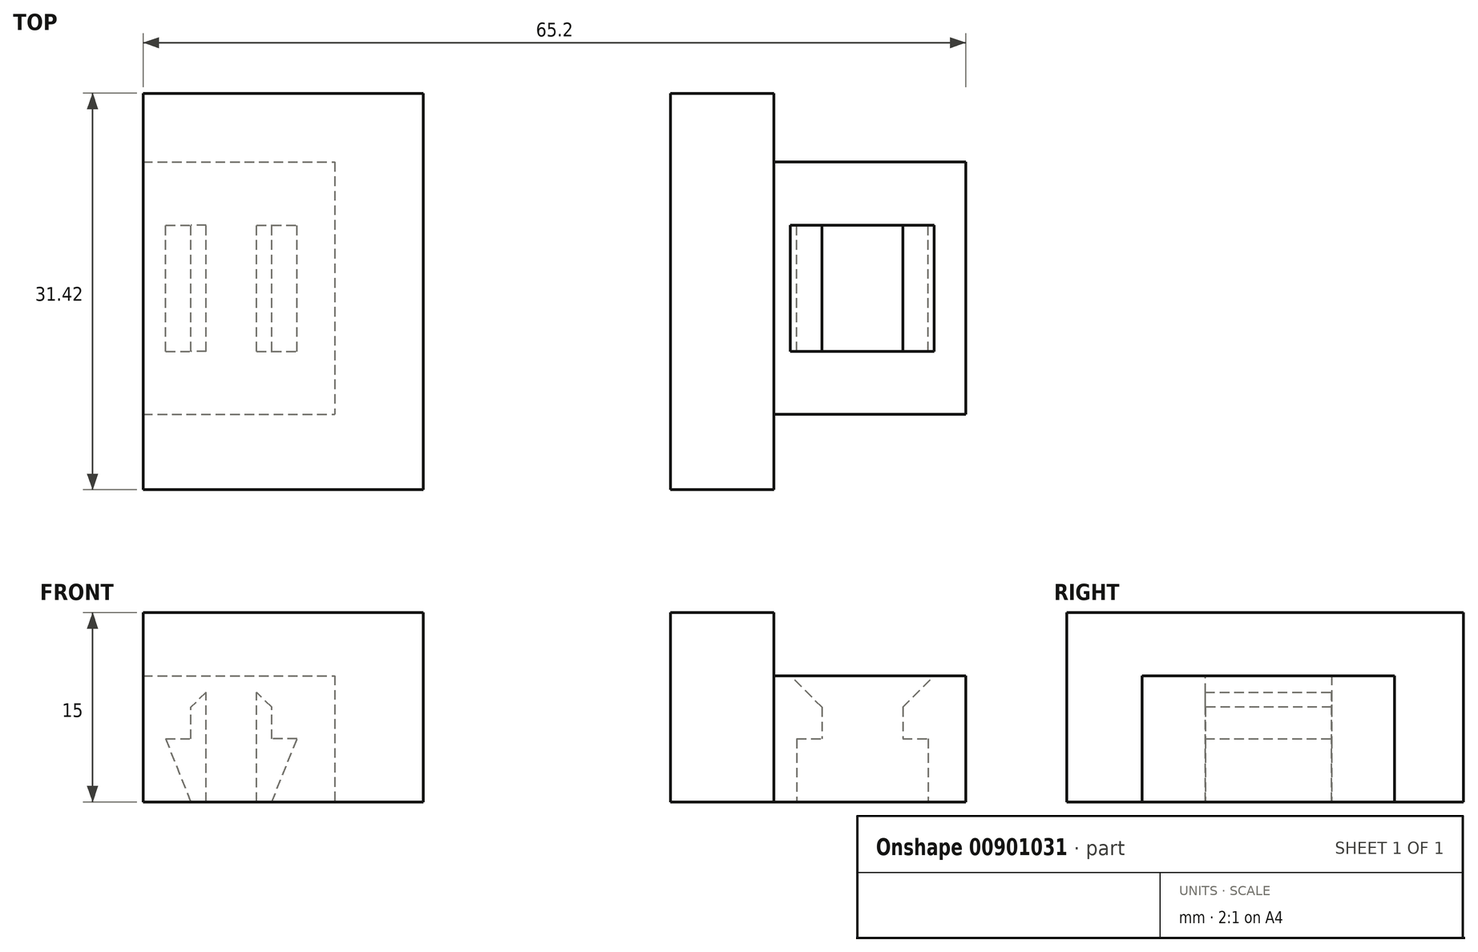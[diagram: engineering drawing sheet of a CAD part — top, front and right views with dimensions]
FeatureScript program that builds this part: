
annotation { "Feature Type Name" : "Feature", "Feature Type Description" : "" }
export const myFeature = defineFeature(function(context is Context, id is Id, definition is map)
    precondition{}
    {
        {
            assignVariable(context, id + "F0", {"name" : "depth", "anyValue" : 10 * mm});
        }
        {
            assignVariable(context, id + "F1", {"name" : "width", "anyValue" : 10 * mm});
        }
        {
            assignVariable(context, id + "F2", {"name" : "front", "anyValue" : 5 * mm});
        }
        {
            var Q0;
            Q0=qCreatedBy(makeId("Front.planeOp"),FACE);
            var sketch = newSketch(context, id + "F3", { "sketchPlane" : qUnion([Q0])});
            skLineSegment(sketch, "E0", {"start": v(0, -1.02) * mm, "end": v(0, 5.37) * mm, "construction": true});
            skLineSegment(sketch, "E1.bottom", {"start": v(-2, 0) * mm, "end": v(-3.2, 0) * mm});
            skLineSegment(sketch, "E1.top", {"start": v(-2, 10) * mm, "end": v(-3.2, 10) * mm});
            skLineSegment(sketch, "E1.left", {"start": v(-2, 0) * mm, "end": v(-2, 10) * mm});
            skLineSegment(sketch, "E1.right", {"start": v(-3.2, 5) * mm, "end": v(-3.2, 10) * mm});
            skLineSegment(sketch, "E2", {"start": v(-3.2, 0) * mm, "end": v(-5.2, 5) * mm});
            skLineSegment(sketch, "E3", {"start": v(-5.2, 5) * mm, "end": v(-3.2, 5) * mm});
            skLineSegment(sketch, "E4.MirrorCS", {"start": v(5.2, 5) * mm, "end": v(3.2, 5) * mm});
            skLineSegment(sketch, "E5.MirrorCS", {"start": v(3.2, 5) * mm, "end": v(3.2, 10) * mm});
            skLineSegment(sketch, "E6.MirrorCS", {"start": v(2, 10) * mm, "end": v(3.2, 10) * mm});
            skLineSegment(sketch, "E7.MirrorCS", {"start": v(2, 0) * mm, "end": v(2, 10) * mm});
            skLineSegment(sketch, "E8.MirrorCS", {"start": v(2, 0) * mm, "end": v(3.2, 0) * mm});
            skLineSegment(sketch, "E9.MirrorCS", {"start": v(3.2, 0) * mm, "end": v(5.2, 5) * mm});
            skSolve(sketch);
        }
        {
            var Q0;
            Q0=makeQuery(id+"F3.imprint","IMPRINT",FACE,{"disambiguationData":[TD([[makeQuery(id+"F3.imprint","IMPRINT",EDGE,{"derivedFrom":sQuery(id+"F3.wireOp",EDGE,"E1.bottom")}),-1.0]])]});
            var Q1;
            Q1=makeQuery(id+"F3.imprint","IMPRINT",FACE,{"disambiguationData":[TD([[makeQuery(id+"F3.imprint","IMPRINT",EDGE,{"derivedFrom":sQuery(id+"F3.wireOp",EDGE,"E4.MirrorCS")}),1.0]])]});
            extrude(context, id + "F4", {"entities" : qUnion([Q0, Q1]), "depth" : getVariable(context, 'width'), "offsetDistance" : 25 * mm});
        }
        {
            var Q0;
            Q0=qCreatedBy(makeId("Top.planeOp"),FACE);
            var sketch = newSketch(context, id + "F5", { "sketchPlane" : qUnion([Q0])});
            skLineSegment(sketch, "E10.0", {"start": v(-3.2, -10) * mm, "end": v(-3.2, 0) * mm});
            skLineSegment(sketch, "E11.0", {"start": v(3.2, -10) * mm, "end": v(3.2, 0) * mm});
            skLineSegment(sketch, "E12", {"start": v(-3.2, 0) * mm, "end": v(3.2, 0) * mm});
            skLineSegment(sketch, "E13", {"start": v(-3.2, -10) * mm, "end": v(3.2, -10) * mm});
            skLineSegment(sketch, "E14.bottom", {"start": v(-7, 5) * mm, "end": v(15.2, 5) * mm});
            skLineSegment(sketch, "E14.top", {"start": v(-7, -15) * mm, "end": v(15.2, -15) * mm});
            skLineSegment(sketch, "E14.left", {"start": v(-7, 5) * mm, "end": v(-7, -15) * mm});
            skLineSegment(sketch, "E14.right", {"start": v(15.2, 5) * mm, "end": v(15.2, -15) * mm});
            skLineSegment(sketch, "E15", {"start": v(8.2, 5) * mm, "end": v(8.2, -15) * mm});
            skLineSegment(sketch, "E16.bottom", {"start": v(-7, 5) * mm, "end": v(-15.2, 5) * mm});
            skLineSegment(sketch, "E16.top", {"start": v(-7, -15.04) * mm, "end": v(-15.2, -15.04) * mm});
            skLineSegment(sketch, "E16.left", {"start": v(-7, 5) * mm, "end": v(-7, -15.04) * mm});
            skLineSegment(sketch, "E16.right", {"start": v(-15.2, 5) * mm, "end": v(-15.2, -15.04) * mm});
            skLineSegment(sketch, "E17.0", {"start": v(-5.2, -10) * mm, "end": v(-5.2, 0) * mm});
            skLineSegment(sketch, "E18.0", {"start": v(5.2, -10) * mm, "end": v(5.2, 0) * mm});
            skLineSegment(sketch, "E19", {"start": v(-5.2, 0) * mm, "end": v(5.2, 0) * mm});
            skLineSegment(sketch, "E20", {"start": v(-5.2, -10) * mm, "end": v(5.2, -10) * mm});
            skLineSegment(sketch, "E21.bottom", {"start": v(15.2, 5) * mm, "end": v(-7, 5) * mm});
            skLineSegment(sketch, "E21.top", {"start": v(15.2, 10.45) * mm, "end": v(-7, 10.45) * mm});
            skLineSegment(sketch, "E21.left", {"start": v(15.2, 5) * mm, "end": v(15.2, 10.45) * mm});
            skLineSegment(sketch, "E21.right", {"start": v(-7, 5) * mm, "end": v(-7, 10.45) * mm});
            skLineSegment(sketch, "E22.bottom", {"start": v(15.2, -15) * mm, "end": v(-7, -15) * mm});
            skLineSegment(sketch, "E22.top", {"start": v(15.2, -20.97) * mm, "end": v(-7, -20.97) * mm});
            skLineSegment(sketch, "E22.left", {"start": v(15.2, -15) * mm, "end": v(15.2, -20.97) * mm});
            skLineSegment(sketch, "E22.right", {"start": v(-7, -15) * mm, "end": v(-7, -20.97) * mm});
            skLineSegment(sketch, "E23.bottom", {"start": v(-15.2, -15.04) * mm, "end": v(-7, -15.04) * mm});
            skLineSegment(sketch, "E23.top", {"start": v(-15.2, -20.97) * mm, "end": v(-7, -20.97) * mm});
            skLineSegment(sketch, "E23.left", {"start": v(-15.2, -15.04) * mm, "end": v(-15.2, -20.97) * mm});
            skLineSegment(sketch, "E23.right", {"start": v(-7, -15.04) * mm, "end": v(-7, -20.97) * mm});
            skLineSegment(sketch, "E24.bottom", {"start": v(-15.2, 5) * mm, "end": v(-7, 5) * mm});
            skLineSegment(sketch, "E24.top", {"start": v(-15.2, 10.45) * mm, "end": v(-7, 10.45) * mm});
            skLineSegment(sketch, "E24.left", {"start": v(-15.2, 5) * mm, "end": v(-15.2, 10.45) * mm});
            skSolve(sketch);
        }
        {
            var Q0;
            {var subQ1=sQuery(id+"F5.wireOp",EDGE,"E12");Q0=makeQuery(id+"F5.imprint","IMPRINT",FACE,{"disambiguationData":[TD([[makeQuery(id+"F5.imprint","IMPRINT",EDGE,{"derivedFrom":subQ1}),1.0]])]});}
            var Q1;
            {var subQ0=sQuery(id+"F5.wireOp",EDGE,"E11.0");Q1=makeQuery(id+"F5.imprint","IMPRINT",FACE,{"disambiguationData":[TD([[makeQuery(id+"F5.imprint","IMPRINT",EDGE,{"derivedFrom":subQ0}),-1.0]])]});}
            var Q2;
            {var subQ0=sQuery(id+"F5.wireOp",EDGE,"E10.0");Q2=makeQuery(id+"F5.imprint","IMPRINT",FACE,{"disambiguationData":[TD([[makeQuery(id+"F5.imprint","IMPRINT",EDGE,{"derivedFrom":subQ0}),1.0]])]});}
            extrude(context, id + "F6", {"entities" : qUnion([Q0, Q1, Q2]), "depth" : getVariable(context, 'depth'), "offsetDistance" : 25 * mm, "hasSecondDirection" : true, "secondDirectionOppositeDirection" : false, "secondDirectionDepth" : getVariable(context, 'depth') / 2});
        }
        {
            var Q0;
            {var subQ1=sQuery(id+"F5.wireOp",EDGE,"E12");Q0=makeQuery(id+"F5.imprint","IMPRINT",FACE,{"disambiguationData":[TD([[makeQuery(id+"F5.imprint","IMPRINT",EDGE,{"derivedFrom":subQ1}),1.0]])]});}
            extrude(context, id + "F7", {"entities" : qUnion([Q0]), "depth" : getVariable(context, 'depth') / 2, "offsetDistance" : 25 * mm});
        }
        {
            var Q0;
            Q0=makeQuery(id+"F5.imprint","IMPRINT",FACE,{"disambiguationData":[TD([[makeQuery(id+"F5.imprint","IMPRINT",EDGE,{"derivedFrom":sQuery(id+"F5.wireOp",EDGE,"E16.top")}),1.0]])]});
            var Q1;
            Q1=makeQuery(id+"F5.imprint","IMPRINT",FACE,{"disambiguationData":[TD([[makeQuery(id+"F5.imprint","IMPRINT",EDGE,{"derivedFrom":sQuery(id+"F5.wireOp",EDGE,"E14.left")}),-1.0]])]});
            var Q2;
            Q2=makeQuery(id+"F5.imprint","IMPRINT",FACE,{"disambiguationData":[TD([[makeQuery(id+"F5.imprint","IMPRINT",EDGE,{"derivedFrom":sQuery(id+"F5.wireOp",EDGE,"E16.bottom")}),-1.0]])]});
            extrude(context, id + "F8", {"entities" : qUnion([Q0, Q1, Q2]), "operationType" : NewBodyOperationType.ADD, "depth" : getVariable(context, 'depth') + getVariable(context, 'front'), "offsetDistance" : 25 * mm});
        }
        {
            var Q0;
            Q0=makeQuery(id+"F6.opExtrude","CAP_EDGE",EDGE,{"disambiguationData":[OSD([sQuery(id+"F5.wireOp",EDGE,"E10.0")])],"isStart":false});
            var Q1;
            Q1=makeQuery(id+"F6.opExtrude","CAP_EDGE",EDGE,{"disambiguationData":[OSD([sQuery(id+"F5.wireOp",EDGE,"E11.0")])],"isStart":false});
            chamfer(context, id + "F9", {"entities" : qUnion([Q0, Q1]), "width" : getVariable(context, 'depth') / 4, "tangentPropagation" : true});
        }
        {
            var Q0;
            Q0=makeQuery(id+"F6.opExtrude","SWEPT_BODY",BODY,{"disambiguationData":[OSD([sQuery(id+"F5.wireOp",EDGE,"E10.0"),sQuery(id+"F5.wireOp",EDGE,"E11.0"),sQuery(id+"F5.wireOp",EDGE,"E12"),sQuery(id+"F5.wireOp",EDGE,"E13"),sQuery(id+"F5.wireOp",EDGE,"E14.bottom"),sQuery(id+"F5.wireOp",EDGE,"E14.top"),sQuery(id+"F5.wireOp",EDGE,"E14.left"),sQuery(id+"F5.wireOp",EDGE,"E15")])]});
            transform(context, id + "F10", {"entities" : qUnion([Q0]), "transformType" : TransformType.TRANSLATION_3D, "dx" : 50 * mm, "dy" : 0 * mm, "dz" : 0 * mm, "makeCopy" : false});
        }
        {
            var Q0;
            {var subQ0=sQuery(id+"F5.wireOp",EDGE,"E14.right");Q0=makeQuery(id+"F5.imprint","IMPRINT",FACE,{"disambiguationData":[TD([[makeQuery(id+"F5.imprint","IMPRINT",EDGE,{"derivedFrom":subQ0}),-1.0]])]});}
            extrude(context, id + "F11", {"entities" : qUnion([Q0]), "depth" : getVariable(context, 'depth') + getVariable(context, 'front'), "offsetDistance" : 25 * mm});
        }
        {
            var Q0;
            {var subQ0=sQuery(id+"F5.wireOp",EDGE,"E10.0");Q0=makeQuery(id+"F5.imprint","IMPRINT",FACE,{"disambiguationData":[TD([[makeQuery(id+"F5.imprint","IMPRINT",EDGE,{"derivedFrom":subQ0}),1.0]])]});}
            var Q1;
            {var subQ1=sQuery(id+"F5.wireOp",EDGE,"E12");Q1=makeQuery(id+"F5.imprint","IMPRINT",FACE,{"disambiguationData":[TD([[makeQuery(id+"F5.imprint","IMPRINT",EDGE,{"derivedFrom":subQ1}),1.0]])]});}
            var Q2;
            {var subQ0=sQuery(id+"F5.wireOp",EDGE,"E11.0");Q2=makeQuery(id+"F5.imprint","IMPRINT",FACE,{"disambiguationData":[TD([[makeQuery(id+"F5.imprint","IMPRINT",EDGE,{"derivedFrom":subQ0}),-1.0]])]});}
            var Q3;
            Q3=makeQuery(id+"F5.imprint","IMPRINT",FACE,{"disambiguationData":[TD([[makeQuery(id+"F5.imprint","IMPRINT",EDGE,{"derivedFrom":sQuery(id+"F5.wireOp",EDGE,"E10.0")}),-1.0]])]});
            extrude(context, id + "F12", {"entities" : qUnion([Q0, Q1, Q2, Q3]), "depth" : getVariable(context, 'depth') + getVariable(context, 'front'), "offsetDistance" : 25 * mm, "hasSecondDirection" : true, "secondDirectionOppositeDirection" : false, "secondDirectionDepth" : getVariable(context, 'depth')});
        }
        {
            var Q0;
            Q0=makeQuery(id+"F4.opExtrude","SWEPT_EDGE",EDGE,{"disambiguationData":[OSD([sQuery(id+"F3.wireOp",EDGE,"E1.top"),sQuery(id+"F3.wireOp",EDGE,"E1.right")])]});
            var Q1;
            Q1=makeQuery(id+"F4.opExtrude","SWEPT_EDGE",EDGE,{"disambiguationData":[OSD([sQuery(id+"F3.wireOp",EDGE,"E5.MirrorCS"),sQuery(id+"F3.wireOp",EDGE,"E6.MirrorCS")])]});
            chamfer(context, id + "F13", {"entities" : qUnion([Q0, Q1]), "width" : getVariable(context, 'depth') / 4, "tangentPropagation" : true});
        }
        {
            var Q0;
            {var subQ0=sQuery(id+"F5.wireOp",EDGE,"E16.left");Q0=makeQuery(id+"F5.imprint","IMPRINT",FACE,{"disambiguationData":[TD([[makeQuery(id+"F5.imprint","IMPRINT",EDGE,{"derivedFrom":subQ0}),1.0]])]});}
            var Q1;
            Q1=makeQuery(id+"F5.imprint","IMPRINT",FACE,{"disambiguationData":[TD([[makeQuery(id+"F5.imprint","IMPRINT",EDGE,{"derivedFrom":sQuery(id+"F5.wireOp",EDGE,"E21.top")}),1.0]])]});
            extrude(context, id + "F14", {"entities" : qUnion([Q0, Q1]), "operationType" : NewBodyOperationType.ADD, "depth" : getVariable(context, 'depth') + getVariable(context, 'front'), "offsetDistance" : 25 * mm});
        }
    });
